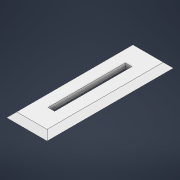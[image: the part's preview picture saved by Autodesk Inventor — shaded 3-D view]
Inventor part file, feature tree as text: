
AUTODESK INVENTOR PART (.ipt)
format: ipt  version: 2022 (Build 260153000, 153)  size: 100,352 bytes
history: native  units: mm
features: other x1, extrude x1, chamfer x1, sketch x1
ambient origin geometry x8: Origin, YZ Plane, XZ Plane, XY Plane, X Axis, Y Axis, Z Axis, Center Point
bodies: Body1 (feature_tree)
feature tree (4):
  other  "ソリッド1"
  extrude  "押し出し1"  Depth=1.3mm
  chamfer  "面取り1"  Distance=15.3mm
  sketch  "スケッチ1"
